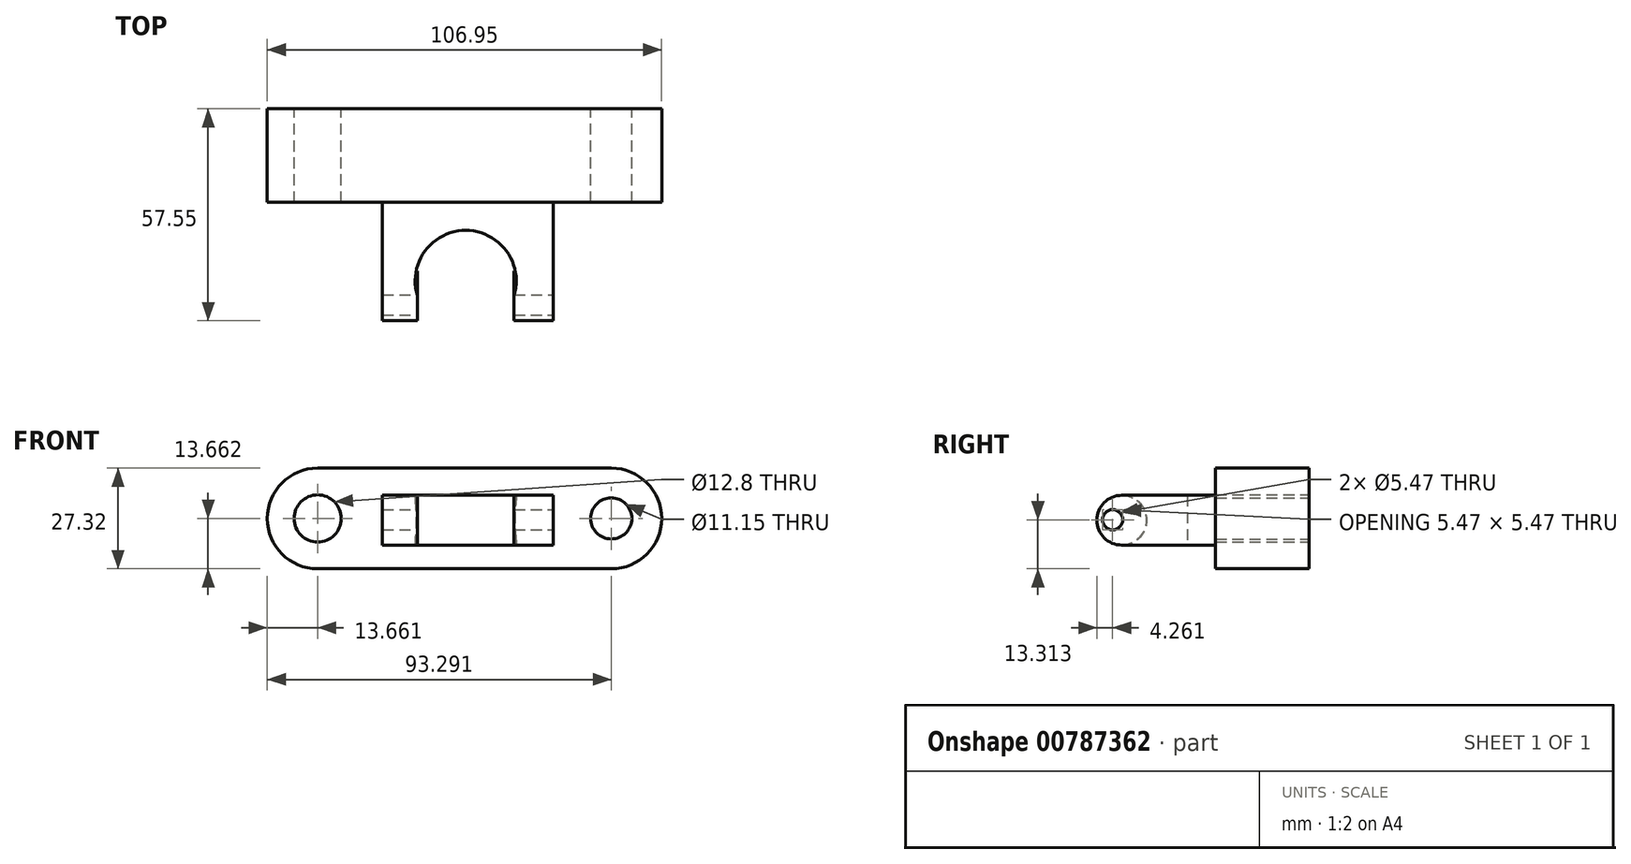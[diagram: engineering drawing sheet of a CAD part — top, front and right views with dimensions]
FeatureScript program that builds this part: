
annotation { "Feature Type Name" : "Feature", "Feature Type Description" : "" }
export const myFeature = defineFeature(function(context is Context, id is Id, definition is map)
    precondition{}
    {
        {
            var Q0;
            Q0=qCreatedBy(makeId("Front.planeOp"),FACE);
            var sketch = newSketch(context, id + "F0", { "sketchPlane" : qUnion([Q0])});
            skLineSegment(sketch, "E0", {"start": v(-35.87, 27.32) * mm, "end": v(43.76, 27.32) * mm});
            skLineSegment(sketch, "E1", {"start": v(43.76, 0) * mm, "end": v(-35.87, 0) * mm});
            skArc(sketch, "E2", {"start": v(-35.87, 27.32) * mm, "mid": v(-49.53, 13.66) * mm, "end": v(-35.87, 0) * mm});
            skArc(sketch, "E3", {"start": v(43.76, 0) * mm, "mid": v(57.42, 13.66) * mm, "end": v(43.76, 27.32) * mm});
            skCircle(sketch, "E4", {"center": v(-35.87, 13.66) * mm, "radius": 6.4 * mm});
            skCircle(sketch, "E5", {"center": v(43.76, 13.66) * mm, "radius": 5.58 * mm});
            skSolve(sketch);
        }
        {
            var Q0;
            Q0 = qSketchRegion(id + "F0", true);
            extrude(context, id + "F1", {"entities" : qUnion([Q0]), "depth" : 25.4 * mm, "offsetDistance" : 25.4 * mm});
        }
        {
            var Q0;
            Q0=makeQuery(id+"F1.opExtrude","CAP_FACE",FACE,{"disambiguationData":[OSD([sQuery(id+"F0.wireOp",EDGE,"E0"),sQuery(id+"F0.wireOp",EDGE,"E1"),sQuery(id+"F0.wireOp",EDGE,"E2"),sQuery(id+"F0.wireOp",EDGE,"E3"),sQuery(id+"F0.wireOp",EDGE,"E4"),sQuery(id+"F0.wireOp",EDGE,"E5")])],"isStart":false});
            var sketch = newSketch(context, id + "F2", { "sketchPlane" : qUnion([Q0])});
            skLineSegment(sketch, "E6.bottom", {"start": v(-18.29, 19.94) * mm, "end": v(28, 19.94) * mm});
            skLineSegment(sketch, "E6.top", {"start": v(-18.29, 6.43) * mm, "end": v(28, 6.43) * mm});
            skLineSegment(sketch, "E6.left", {"start": v(-18.29, 19.94) * mm, "end": v(-18.29, 6.43) * mm});
            skLineSegment(sketch, "E6.right", {"start": v(28, 19.94) * mm, "end": v(28, 6.43) * mm});
            skSolve(sketch);
        }
        {
            var Q0;
            Q0=makeQuery(id+"F2.imprint","IMPRINT",FACE,{"disambiguationData":[TD([[makeQuery(id+"F2.imprint","IMPRINT",EDGE,{"derivedFrom":sQuery(id+"F2.wireOp",EDGE,"E6.bottom")}),-1.0]])]});
            extrude(context, id + "F3", {"entities" : qUnion([Q0]), "operationType" : NewBodyOperationType.ADD, "depth" : 25.4 * mm, "offsetDistance" : 25.4 * mm});
        }
        {
            var Q0;
            Q0=makeQuery(id+"F3.opExtrude","SWEPT_FACE",FACE,{"disambiguationData":[OSD([sQuery(id+"F2.wireOp",EDGE,"E6.top")])]});
            var sketch = newSketch(context, id + "F4", { "sketchPlane" : qUnion([Q0])});
            skArc(sketch, "E7", {"start": v(-8.78, 50.8) * mm, "mid": v(4.29, 33.02) * mm, "end": v(17.36, 50.8) * mm});
            skSolve(sketch);
        }
        {
            var Q0;
            {var subQ0=sQuery(id+"F4.wireOp",EDGE,"E7");Q0=makeQuery(id+"F4.imprint","IMPRINT",FACE,{"disambiguationData":[TD([[makeQuery(id+"F4.imprint","IMPRINT",EDGE,{"derivedFrom":subQ0}),1.0]])]});}
            extrude(context, id + "F5", {"entities" : qUnion([Q0]), "operationType" : NewBodyOperationType.REMOVE, "oppositeDirection" : true, "depth" : 69.34 * mm, "offsetDistance" : 25.4 * mm});
        }
        {
            var Q0;
            {var subQ0=sQuery(id+"F2.wireOp",EDGE,"E6.bottom");var subQ1=sQuery(id+"F2.wireOp",EDGE,"E6.top");var subQ2=sQuery(id+"F2.wireOp",EDGE,"E6.left");Q0=makeQuery(id+"F5.boolean.opBoolean","SPLIT",FACE,{"disambiguationData":[TD([makeQuery(id+"F3.opExtrude","SWEPT_FACE",FACE,{"disambiguationData":[OSD([subQ2])]})])],"derivedFrom":makeQuery(id+"F3.opExtrude","CAP_FACE",FACE,{"disambiguationData":[OSD([subQ0,subQ1,subQ2,sQuery(id+"F2.wireOp",EDGE,"E6.right")])],"isStart":false})});}
            var sketch = newSketch(context, id + "F6", { "sketchPlane" : qUnion([Q0])});
            skLineSegment(sketch, "E8", {"start": v(-18.29, 13.19) * mm, "end": v(-8.78, 13.19) * mm});
            skSolve(sketch);
        }
        {
            var Q0;
            {var subQ0=sQuery(id+"F2.wireOp",EDGE,"E6.bottom");var subQ1=sQuery(id+"F2.wireOp",EDGE,"E6.right");var subQ2=sQuery(id+"F2.wireOp",EDGE,"E6.top");Q0=makeQuery(id+"F5.boolean.opBoolean","SPLIT",FACE,{"disambiguationData":[TD([makeQuery(id+"F3.opExtrude","SWEPT_FACE",FACE,{"disambiguationData":[OSD([subQ1])]})])],"derivedFrom":makeQuery(id+"F3.opExtrude","CAP_FACE",FACE,{"disambiguationData":[OSD([subQ0,subQ2,sQuery(id+"F2.wireOp",EDGE,"E6.left"),subQ1])],"isStart":false})});}
            var sketch = newSketch(context, id + "F7", { "sketchPlane" : qUnion([Q0])});
            skLineSegment(sketch, "E9", {"start": v(17.36, 13.19) * mm, "end": v(28, 13.19) * mm});
            skSolve(sketch);
        }
        {
            var Q0;
            Q0 = qSketchRegion(id + "F7", true);
            var Q1;
            {var subQ0=sQuery(id+"F6.wireOp",EDGE,"E8");Q1=makeQuery(id+"F6.imprint","IMPRINT",FACE,{"disambiguationData":[TD([[makeQuery(id+"F6.imprint","IMPRINT",EDGE,{"derivedFrom":subQ0}),-1.0]])]});}
            var Q2;
            Q2=sQuery(id+"F6.wireOp",EDGE,"E8");
            revolve(context, id + "F8", {"operationType" : NewBodyOperationType.ADD, "surfaceOperationType" : NewSurfaceOperationType.NEW, "entities" : qUnion([Q0, Q1]), "axis" : qUnion([Q2]), "revolveType" : RevolveType.FULL});
        }
        {
            var Q0;
            {var subQ0=sQuery(id+"F7.wireOp",EDGE,"E9");Q0=makeQuery(id+"F7.imprint","IMPRINT",FACE,{"disambiguationData":[TD([[makeQuery(id+"F7.imprint","IMPRINT",EDGE,{"derivedFrom":subQ0}),-1.0]])]});}
            var Q1;
            Q1=sQuery(id+"F7.wireOp",EDGE,"E9");
            revolve(context, id + "F9", {"operationType" : NewBodyOperationType.ADD, "surfaceOperationType" : NewSurfaceOperationType.NEW, "entities" : qUnion([Q0]), "axis" : qUnion([Q1]), "revolveType" : RevolveType.FULL});
        }
        {
            var Q0;
            {var subQ0=sQuery(id+"F2.wireOp",EDGE,"E6.right");Q0=makeQuery(id+"F9.boolean.opBoolean","MERGE",FACE,{"derivedFrom":[makeQuery(id+"F3.opExtrude","SWEPT_FACE",FACE,{"disambiguationData":[OSD([subQ0])]}),makeQuery(id+"F9.opRevolve","SWEPT_FACE",FACE,{"disambiguationData":[OSD([subQ0])]})]});}
            var sketch = newSketch(context, id + "F10", { "sketchPlane" : qUnion([Q0])});
            skCircle(sketch, "E10", {"center": v(-53.29, 13.31) * mm, "radius": 2.73 * mm});
            skSolve(sketch);
        }
        {
            var Q0;
            Q0 = qSketchRegion(id + "F10", true);
            extrude(context, id + "F11", {"entities" : qUnion([Q0]), "operationType" : NewBodyOperationType.REMOVE, "oppositeDirection" : true, "depth" : 182.63 * mm, "offsetDistance" : 25.4 * mm});
        }
    });
